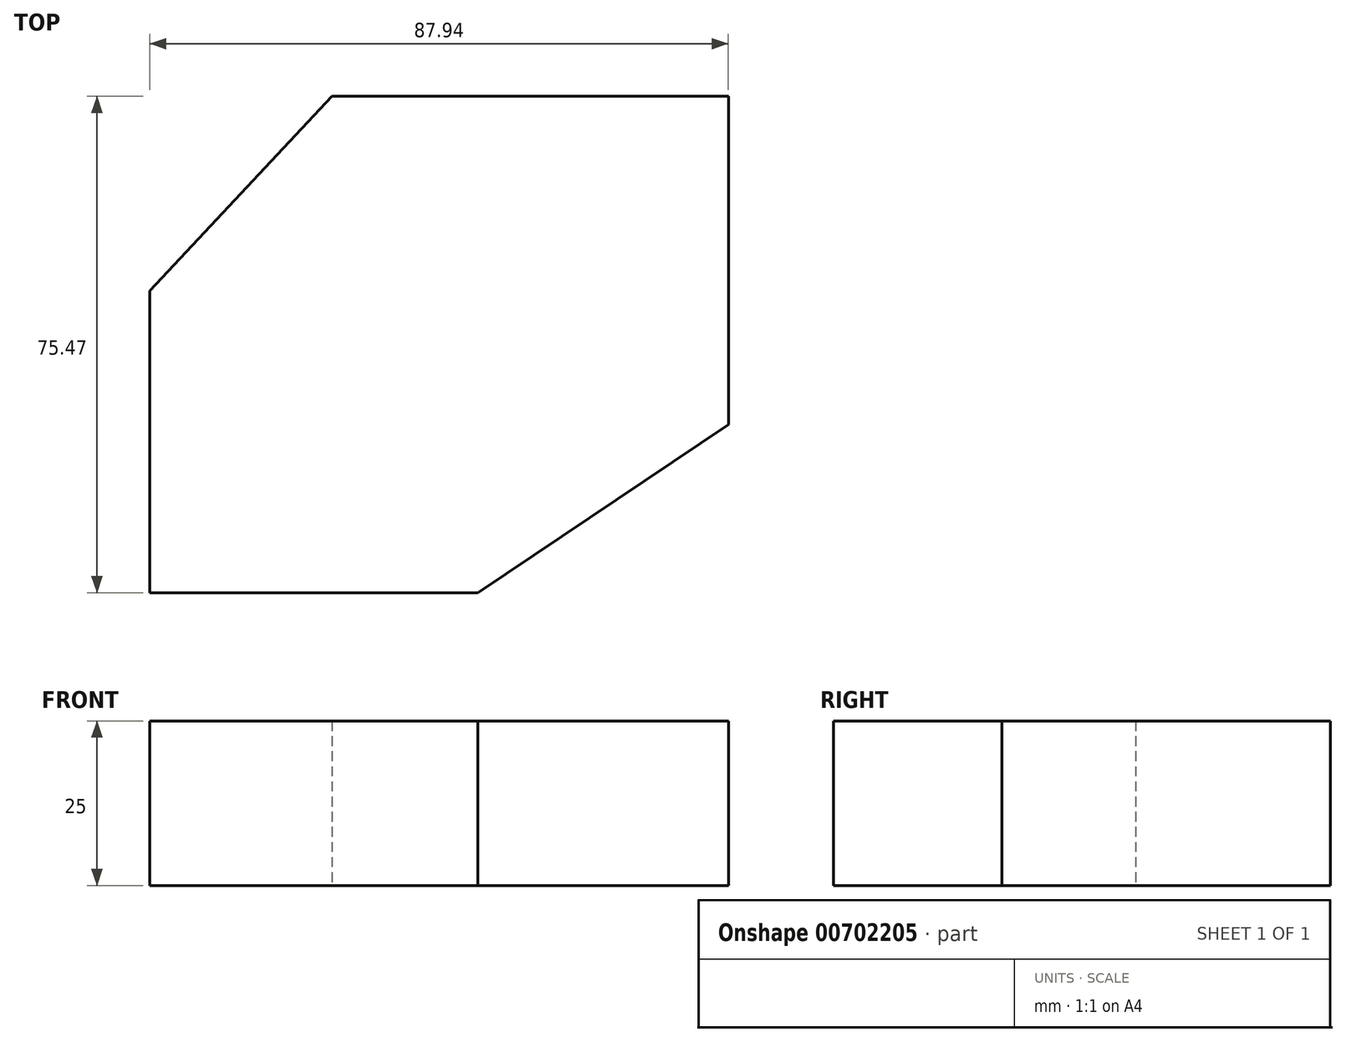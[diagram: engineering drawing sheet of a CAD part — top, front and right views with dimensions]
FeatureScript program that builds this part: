
annotation { "Feature Type Name" : "Feature", "Feature Type Description" : "" }
export const myFeature = defineFeature(function(context is Context, id is Id, definition is map)
    precondition{}
    {
        {
            var Q0;
            Q0=qCreatedBy(makeId("Top.planeOp"),FACE);
            var sketch = newSketch(context, id + "F0", { "sketchPlane" : qUnion([Q0])});
            skLineSegment(sketch, "E0.bottom", {"start": v(-35.62, 38.27) * mm, "end": v(14.27, 38.27) * mm});
            skLineSegment(sketch, "E0.top", {"start": v(-35.62, -7.61) * mm, "end": v(14.27, -7.61) * mm});
            skLineSegment(sketch, "E0.left", {"start": v(-35.62, 38.27) * mm, "end": v(-35.62, -7.61) * mm});
            skLineSegment(sketch, "E0.right", {"start": v(14.27, 38.27) * mm, "end": v(14.27, -7.61) * mm});
            skLineSegment(sketch, "E1", {"start": v(14.27, 38.27) * mm, "end": v(52.32, 67.86) * mm});
            skLineSegment(sketch, "E2", {"start": v(52.32, 67.86) * mm, "end": v(52.32, 17.97) * mm});
            skLineSegment(sketch, "E3", {"start": v(52.32, 17.97) * mm, "end": v(14.27, -7.61) * mm});
            skLineSegment(sketch, "E4", {"start": v(52.32, 67.86) * mm, "end": v(-7.93, 67.86) * mm});
            skLineSegment(sketch, "E5", {"start": v(-7.93, 67.86) * mm, "end": v(-35.62, 38.27) * mm});
            skSolve(sketch);
        }
        {
            var Q0;
            Q0 = qSketchRegion(id + "F0", true);
            extrude(context, id + "F1", {"entities" : qUnion([Q0]), "depth" : 25 * mm, "offsetDistance" : 25 * mm});
        }
    });
